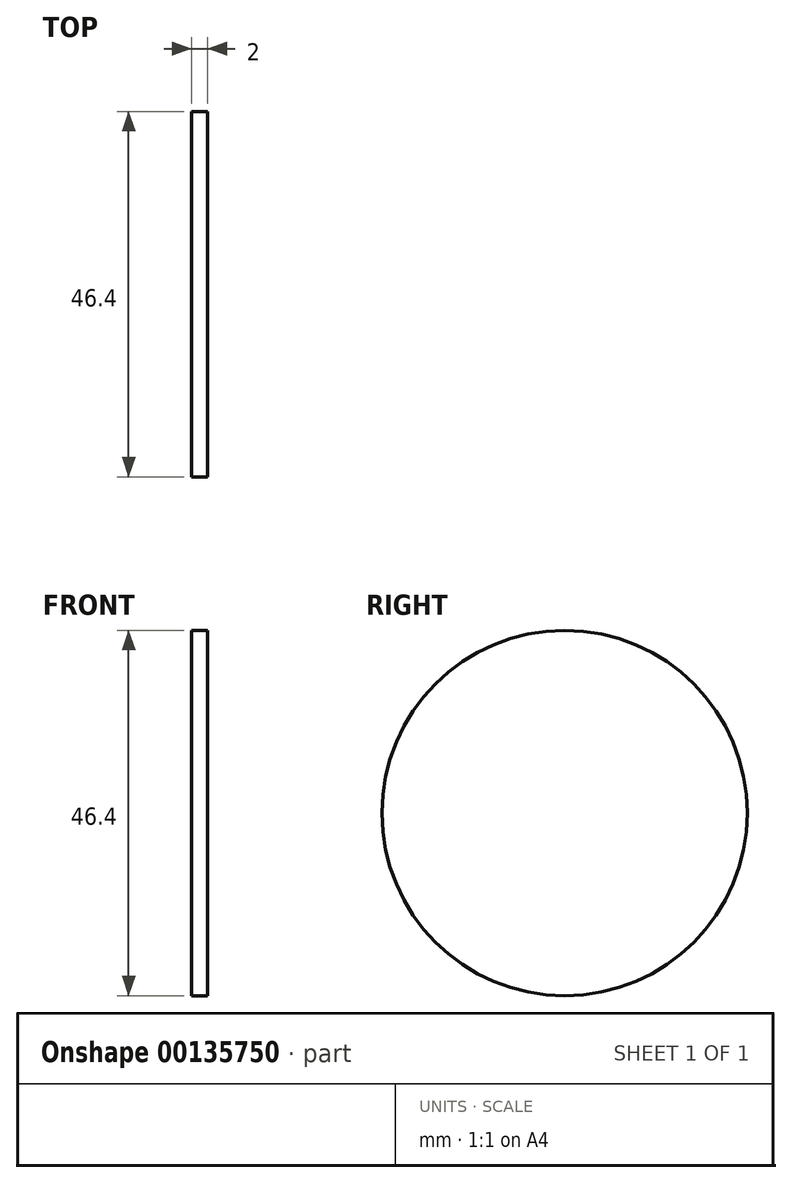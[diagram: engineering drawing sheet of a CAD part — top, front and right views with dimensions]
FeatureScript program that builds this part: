
annotation { "Feature Type Name" : "Feature", "Feature Type Description" : "" }
export const myFeature = defineFeature(function(context is Context, id is Id, definition is map)
    precondition{}
    {
        {
            var Q0;
            Q0=qCreatedBy(makeId("Right.planeOp"),FACE);
            var sketch = newSketch(context, id + "F0", { "sketchPlane" : qUnion([Q0])});
            skCircle(sketch, "E0", {"center": v(0, 0) * mm, "radius": 23.2 * mm});
            skSolve(sketch);
        }
        {
            var Q0;
            Q0=makeQuery(id+"F0.imprint","IMPRINT",FACE,{"disambiguationData":[TD([[makeQuery(id+"F0.imprint","IMPRINT",EDGE,{"derivedFrom":sQuery(id+"F0.wireOp",EDGE,"E0")}),1.0]])]});
            extrude(context, id + "F1", {"entities" : qUnion([Q0]), "depth" : 2 * mm});
        }
    });
